# Revit family: Towel_Ring-American_Standard-Traditional_Series-8334190_Series
name_source: partatom
category: Specialty Equipment
units: mm (PartAtom-declared; Revit-internal decimal feet)

## family parameters
Cut with Voids When Loaded = No
Host = Face
OmniClass Number = 23.40.20.21.27
OmniClass Title = Towel Bars
Part Type = Normal
Room Calculation Point = No
Round Connector Dimension = Use Diameter
Shared = Yes

## types (2) — shared parameters
Default Elevation = 40"
Description = TR Series Towel Ring
Height = 8 1/4"
Installation Type = Wall Mounted
Length = 3 3/4"
Manufacturer = American Standard
Price = Prices may vary. Please consult Manufacturer Representative for most up-to-date price list.
Product Documentation Link = https://americanstandard.box.com
Product Page URL = https://www.americanstandard-us.com
Revised Date = 02/22/2022
Type Comments = Traditional
URL = http://www.americanstandard-us.com
Warranty Information = 1 Year Warranty
Width = 7 1/8"

## per-type parameters (varying)
| type | Assembly Code | Finish | Material |
| 8334190.002 | C1030200 | Metal-American Standard-002-Polished Chrome | Metal-American Standard-002-Polished Chrome |
| 8334190.295 | C1030220 | Metal-American Standard-295-Satin Nickel | Metal-American Standard-295-Satin Nickel |

note: column(s) folded — value = type name in every type: Model

## geometry (parser evidence)
native form markers: Sweep x3
no freeform markers — native parametric forms only
